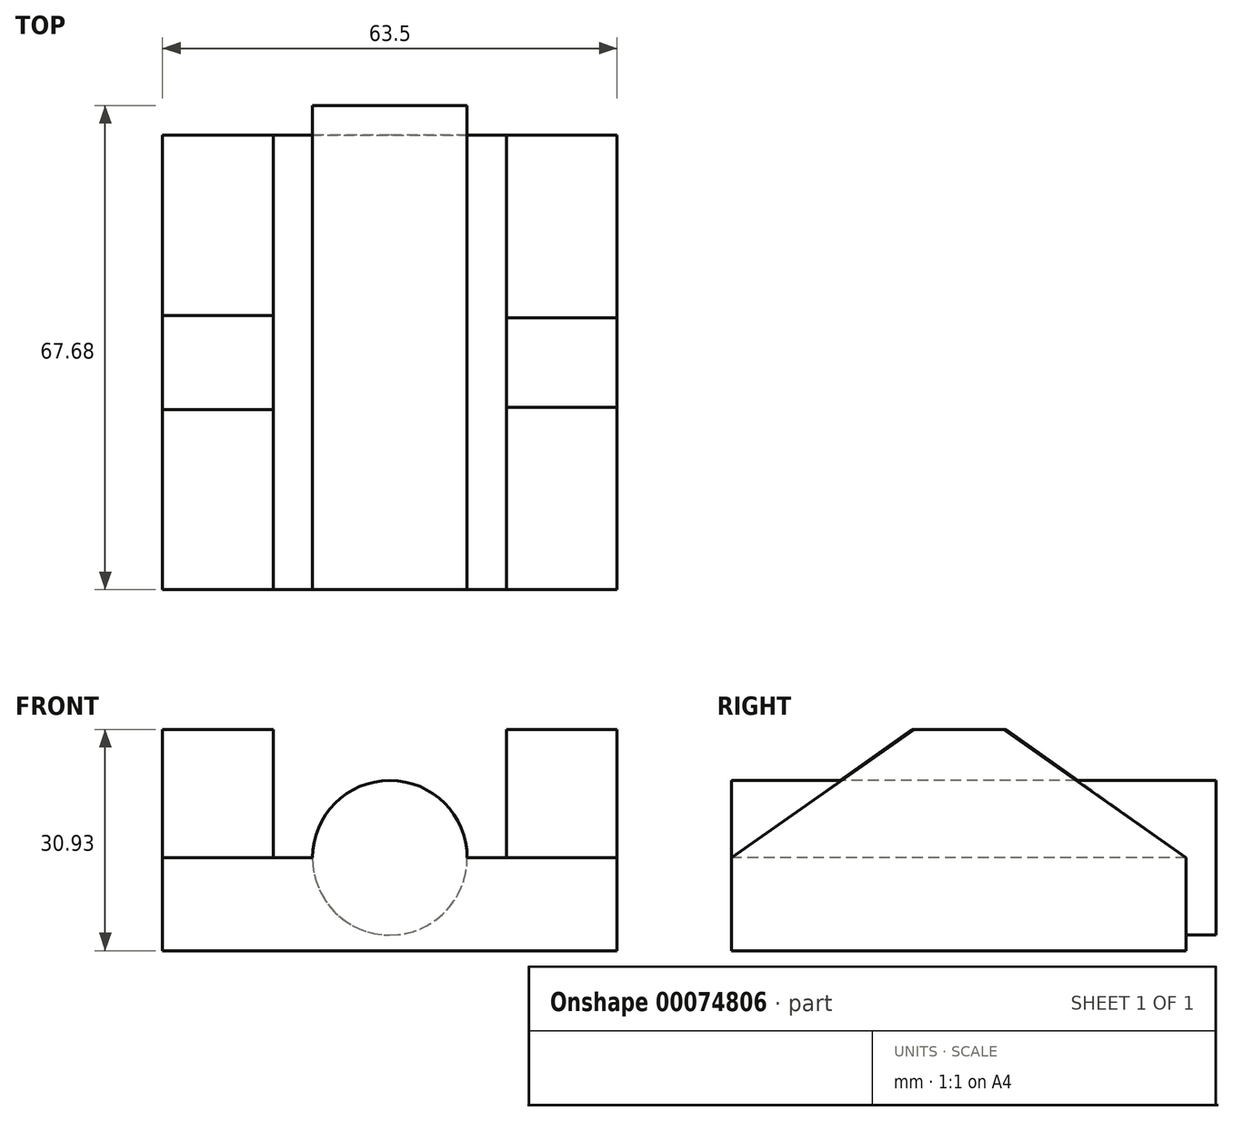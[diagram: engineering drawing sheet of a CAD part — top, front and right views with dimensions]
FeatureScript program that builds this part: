
annotation { "Feature Type Name" : "Feature", "Feature Type Description" : "" }
export const myFeature = defineFeature(function(context is Context, id is Id, definition is map)
    precondition{}
    {
        {
            var Q0;
            Q0=qCreatedBy(makeId("Top.planeOp"),FACE);
            var sketch = newSketch(context, id + "F0", { "sketchPlane" : qUnion([Q0])});
            skLineSegment(sketch, "E0.rect.bottom", {"start": v(-31.75, 31.75) * mm, "end": v(31.75, 31.75) * mm});
            skLineSegment(sketch, "E0.rect.top", {"start": v(-31.75, -31.75) * mm, "end": v(31.75, -31.75) * mm});
            skLineSegment(sketch, "E0.rect.left", {"start": v(-31.75, 31.75) * mm, "end": v(-31.75, -31.75) * mm});
            skLineSegment(sketch, "E0.rect.right", {"start": v(31.75, 31.75) * mm, "end": v(31.75, -31.75) * mm});
            skPoint(sketch, "E0.rect.middle", {"position": v(0, 0) * mm});
            skSolve(sketch);
        }
        {
            var Q0;
            Q0 = qSketchRegion(id + "F0", true);
            extrude(context, id + "F1", {"entities" : qUnion([Q0]), "depth" : 12.98 * mm});
        }
        {
            var Q0;
            Q0=makeQuery(id+"F1.opExtrude","SWEPT_FACE",FACE,{"disambiguationData":[OSD([sQuery(id+"F0.wireOp",EDGE,"E0.rect.left")])]});
            var sketch = newSketch(context, id + "F2", { "sketchPlane" : qUnion([Q0])});
            skLineSegment(sketch, "E1", {"start": v(-31.75, 12.98) * mm, "end": v(-6.56, 30.93) * mm});
            skPoint(sketch, "E2", {"position": v(31.75, 12.98) * mm});
            skPoint(sketch, "E3.MirrorP", {"position": v(-11, 73) * mm});
            skLineSegment(sketch, "E4.MirrorCS", {"start": v(31.75, 12.98) * mm, "end": v(6.56, 30.93) * mm});
            skLineSegment(sketch, "E5", {"start": v(-6.56, 30.93) * mm, "end": v(6.56, 30.93) * mm});
            skSolve(sketch);
        }
        {
            var Q0;
            Q0 = qSketchRegion(id + "F2", true);
            var Q1;
            Q1=makeQuery(id+"F2.imprint","IMPRINT",FACE,{"disambiguationData":[TD([[makeQuery(id+"F2.imprint","IMPRINT",EDGE,{"derivedFrom":sQuery(id+"F2.wireOp",EDGE,"E1")}),-1.0]])]});
            extrude(context, id + "F3", {"entities" : qUnion([Q0, Q1]), "oppositeDirection" : true, "depth" : 15.44 * mm});
        }
        {
            var Q0;
            Q0=makeQuery(id+"F1.opExtrude","SWEPT_FACE",FACE,{"disambiguationData":[OSD([sQuery(id+"F0.wireOp",EDGE,"E0.rect.right")])]});
            var sketch = newSketch(context, id + "F4", { "sketchPlane" : qUnion([Q0])});
            skLineSegment(sketch, "E6", {"start": v(-31.75, 12.98) * mm, "end": v(-6.26, 30.93) * mm});
            skLineSegment(sketch, "E7.MirrorCS", {"start": v(31.75, 12.98) * mm, "end": v(6.26, 30.93) * mm});
            skLineSegment(sketch, "E8", {"start": v(-6.26, 30.93) * mm, "end": v(6.26, 30.93) * mm});
            skSolve(sketch);
        }
        {
            var Q0;
            Q0 = qSketchRegion(id + "F4", true);
            var Q1;
            Q1=makeQuery(id+"F4.imprint","IMPRINT",FACE,{"disambiguationData":[TD([[makeQuery(id+"F4.imprint","IMPRINT",EDGE,{"derivedFrom":sQuery(id+"F4.wireOp",EDGE,"E6")}),-1.0]])]});
            extrude(context, id + "F5", {"entities" : qUnion([Q0, Q1]), "operationType" : NewBodyOperationType.ADD, "oppositeDirection" : true, "depth" : 15.44 * mm});
        }
        {
            var Q0;
            Q0=makeQuery(id+"F1.opExtrude","SWEPT_FACE",FACE,{"disambiguationData":[OSD([sQuery(id+"F0.wireOp",EDGE,"E0.rect.top")])]});
            var sketch = newSketch(context, id + "F6", { "sketchPlane" : qUnion([Q0])});
            skCircle(sketch, "E9", {"center": v(0, 12.98) * mm, "radius": 10.8 * mm});
            skSolve(sketch);
        }
        {
            var Q0;
            Q0 = qSketchRegion(id + "F6", true);
            extrude(context, id + "F7", {"entities" : qUnion([Q0]), "operationType" : NewBodyOperationType.ADD, "oppositeDirection" : true, "depth" : 67.68 * mm});
        }
    });
